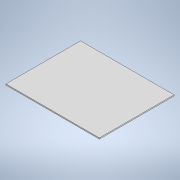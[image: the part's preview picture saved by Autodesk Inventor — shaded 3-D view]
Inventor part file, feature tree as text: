
AUTODESK INVENTOR PART (.ipt)
format: ipt  version: 2022 (Build 260153000, 153)  size: 90,112 bytes
history: native  units: mm
features: extrude x1, sketch x1
ambient origin geometry x8: Origin, YZ Plane, XZ Plane, XY Plane, X Axis, Y Axis, Z Axis, Center Point
bodies: Solid1 (feature_tree)
feature tree (2):
  extrude  "Extrusion1"  Depth=83.0mm
  sketch  "Sketch1"  dims[d0=104.0mm d1=83.0mm d2=1.25mm d3=0.0mm]
